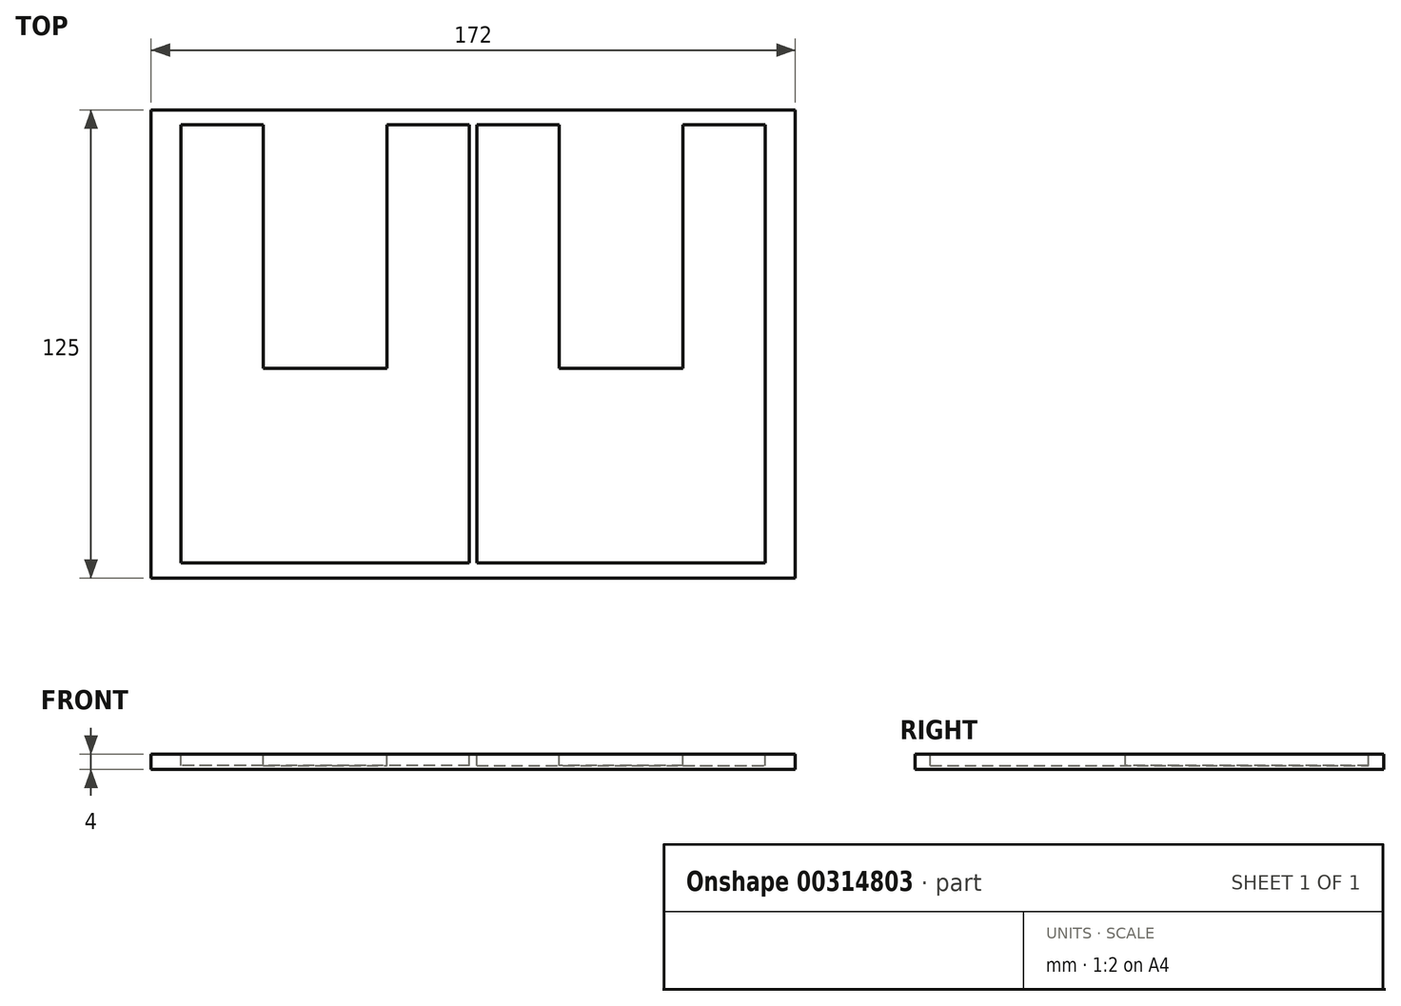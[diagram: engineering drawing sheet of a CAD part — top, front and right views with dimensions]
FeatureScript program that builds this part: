
annotation { "Feature Type Name" : "Feature", "Feature Type Description" : "" }
export const myFeature = defineFeature(function(context is Context, id is Id, definition is map)
    precondition{}
    {
        {
            var Q0;
            Q0=qCreatedBy(makeId("Top.planeOp"),FACE);
            var sketch = newSketch(context, id + "F0", { "sketchPlane" : qUnion([Q0])});
            skLineSegment(sketch, "E0.bottom", {"start": v(2, -57.47) * mm, "end": v(77, -57.47) * mm});
            skLineSegment(sketch, "E0.top", {"start": v(2, 57.53) * mm, "end": v(22, 57.53) * mm});
            skLineSegment(sketch, "E0.left", {"start": v(2, -57.47) * mm, "end": v(2, 57.53) * mm});
            skPoint(sketch, "E0.middle", {"position": v(39.5, 0.03) * mm});
            skLineSegment(sketch, "E1.bottom", {"start": v(77, 57.53) * mm, "end": v(57, 57.53) * mm});
            skLineSegment(sketch, "E1.right", {"start": v(57, 57.53) * mm, "end": v(57, -7.47) * mm});
            skLineSegment(sketch, "E2.left", {"start": v(2, 57.53) * mm, "end": v(2, -7.5) * mm});
            skLineSegment(sketch, "E2.right", {"start": v(22, 57.53) * mm, "end": v(22, -7.47) * mm});
            skLineSegment(sketch, "E3", {"start": v(57, -7.47) * mm, "end": v(22, -7.47) * mm});
            skLineSegment(sketch, "E4.trimOffspring", {"start": v(57, 57.53) * mm, "end": v(77, 57.53) * mm});
            skLineSegment(sketch, "E5", {"start": v(77, 57.53) * mm, "end": v(77, -57.47) * mm});
            skLineSegment(sketch, "E6.0", {"start": v(1, -58.47) * mm, "end": v(78, -58.47) * mm});
            skLineSegment(sketch, "E6.1", {"start": v(78, 58.53) * mm, "end": v(78, -58.47) * mm});
            skLineSegment(sketch, "E6.2", {"start": v(1, -58.47) * mm, "end": v(1, 58.53) * mm});
            skLineSegment(sketch, "E6.3", {"start": v(56, 58.53) * mm, "end": v(78, 58.53) * mm});
            skLineSegment(sketch, "E6.4", {"start": v(1, 58.53) * mm, "end": v(23, 58.53) * mm});
            skLineSegment(sketch, "E6.5", {"start": v(23, 58.53) * mm, "end": v(23, -6.47) * mm});
            skLineSegment(sketch, "E6.6", {"start": v(56, -6.47) * mm, "end": v(23, -6.47) * mm});
            skLineSegment(sketch, "E6.7", {"start": v(56, 58.53) * mm, "end": v(56, -6.47) * mm});
            skLineSegment(sketch, "E7.MirrorCS", {"start": v(-77, 57.53) * mm, "end": v(-57, 57.53) * mm});
            skLineSegment(sketch, "E8.MirrorCS", {"start": v(-2, 57.53) * mm, "end": v(-22, 57.53) * mm});
            skLineSegment(sketch, "E9.MirrorCS", {"start": v(-23, 58.53) * mm, "end": v(-23, -6.47) * mm});
            skLineSegment(sketch, "E10.MirrorCS", {"start": v(-56, 58.53) * mm, "end": v(-56, -6.47) * mm});
            skLineSegment(sketch, "E11.MirrorCS", {"start": v(-78, 58.53) * mm, "end": v(-78, -58.47) * mm});
            skLineSegment(sketch, "E12.MirrorCS", {"start": v(-1, -58.47) * mm, "end": v(-78, -58.47) * mm});
            skLineSegment(sketch, "E13.MirrorCS", {"start": v(-77, 57.53) * mm, "end": v(-77, -57.47) * mm});
            skLineSegment(sketch, "E14.MirrorCS", {"start": v(-57, 57.53) * mm, "end": v(-77, 57.53) * mm});
            skLineSegment(sketch, "E15.MirrorCS", {"start": v(-57, -7.47) * mm, "end": v(-22, -7.47) * mm});
            skLineSegment(sketch, "E16.MirrorCS", {"start": v(-22, 57.53) * mm, "end": v(-22, -7.47) * mm});
            skLineSegment(sketch, "E17.MirrorCS", {"start": v(-2, 57.53) * mm, "end": v(-2, -7.5) * mm});
            skLineSegment(sketch, "E18.MirrorCS", {"start": v(-2, -57.47) * mm, "end": v(-2, 57.53) * mm});
            skLineSegment(sketch, "E19.MirrorCS", {"start": v(-2, -57.47) * mm, "end": v(-77, -57.47) * mm});
            skLineSegment(sketch, "E20.MirrorCS", {"start": v(-1, -58.47) * mm, "end": v(-1, 58.53) * mm});
            skLineSegment(sketch, "E21.MirrorCS", {"start": v(-57, 57.53) * mm, "end": v(-57, -7.47) * mm});
            skLineSegment(sketch, "E22.MirrorCS", {"start": v(-56, 58.53) * mm, "end": v(-78, 58.53) * mm});
            skLineSegment(sketch, "E23.MirrorCS", {"start": v(-1, 58.53) * mm, "end": v(-23, 58.53) * mm});
            skPoint(sketch, "E24.MirrorP", {"position": v(-39.5, 0.03) * mm});
            skLineSegment(sketch, "E25.MirrorCS", {"start": v(-56, -6.47) * mm, "end": v(-23, -6.47) * mm});
            skSolve(sketch);
        }
        {
            var Q0;
            Q0=qCreatedBy(makeId("Top.planeOp"),FACE);
            var sketch = newSketch(context, id + "F1", { "sketchPlane" : qUnion([Q0])});
            skLineSegment(sketch, "E26.bottom", {"start": v(86, -62.5) * mm, "end": v(-86, -62.5) * mm});
            skLineSegment(sketch, "E26.top", {"start": v(86, 62.5) * mm, "end": v(-86, 62.5) * mm});
            skLineSegment(sketch, "E26.left", {"start": v(86, -62.5) * mm, "end": v(86, 62.5) * mm});
            skLineSegment(sketch, "E26.right", {"start": v(-86, -62.5) * mm, "end": v(-86, 62.5) * mm});
            skPoint(sketch, "E26.middle", {"position": v(0, 0) * mm});
            skSolve(sketch);
        }
        {
            var Q0;
            Q0 = qSketchRegion(id + "F1", true);
            extrude(context, id + "F2", {"entities" : qUnion([Q0]), "depth" : -4 * mm});
        }
        {
            var Q0;
            Q0=makeQuery(id+"F0.imprint","IMPRINT",FACE,{"disambiguationData":[TD([[makeQuery(id+"F0.imprint","IMPRINT",EDGE,{"derivedFrom":sQuery(id+"F0.wireOp",EDGE,"E13.MirrorCS")}),1.0]])]});
            var Q1;
            Q1=makeQuery(id+"F0.imprint","IMPRINT",FACE,{"disambiguationData":[TD([[makeQuery(id+"F0.imprint","IMPRINT",EDGE,{"derivedFrom":sQuery(id+"F0.wireOp",EDGE,"E0.bottom")}),1.0]])]});
            var Q2;
            Q2=makeQuery(id+"F0.imprint","IMPRINT",FACE,{"disambiguationData":[TD([[makeQuery(id+"F0.imprint","IMPRINT",EDGE,{"derivedFrom":sQuery(id+"F0.wireOp",EDGE,"E9.MirrorCS")}),1.0]])]});
            var Q3;
            Q3=makeQuery(id+"F0.imprint","IMPRINT",FACE,{"disambiguationData":[TD([[makeQuery(id+"F0.imprint","IMPRINT",EDGE,{"derivedFrom":sQuery(id+"F0.wireOp",EDGE,"E0.bottom")}),-1.0]])]});
            extrude(context, id + "F3", {"entities" : qUnion([Q0, Q1, Q2, Q3]), "operationType" : NewBodyOperationType.REMOVE, "oppositeDirection" : true, "depth" : 3 * mm});
        }
    });
